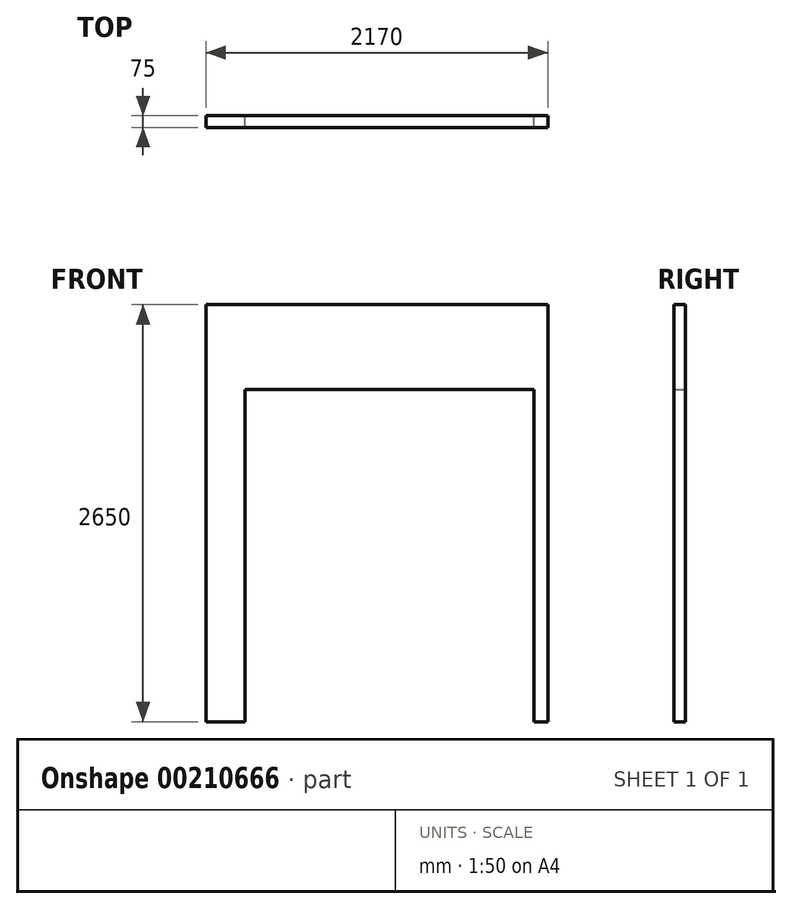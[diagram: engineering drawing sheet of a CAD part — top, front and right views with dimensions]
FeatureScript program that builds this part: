
annotation { "Feature Type Name" : "Feature", "Feature Type Description" : "" }
export const myFeature = defineFeature(function(context is Context, id is Id, definition is map)
    precondition{}
    {
        {
            var Q0;
            Q0=qCreatedBy(makeId("Front.planeOp"),FACE);
            var sketch = newSketch(context, id + "F0", { "sketchPlane" : qUnion([Q0])});
            skLineSegment(sketch, "E0.bottom", {"start": v(0, 0) * mm, "end": v(2170, 0) * mm});
            skLineSegment(sketch, "E0.top", {"start": v(0, 2650) * mm, "end": v(2170, 2650) * mm});
            skLineSegment(sketch, "E0.left", {"start": v(0, 0) * mm, "end": v(0, 2650) * mm});
            skLineSegment(sketch, "E0.right", {"start": v(2170, 0) * mm, "end": v(2170, 2650) * mm});
            skLineSegment(sketch, "E1.bottom", {"start": v(248, 0) * mm, "end": v(2082, 0) * mm});
            skLineSegment(sketch, "E1.top", {"start": v(248, 2110) * mm, "end": v(2082, 2110) * mm});
            skLineSegment(sketch, "E1.left", {"start": v(248, 0) * mm, "end": v(248, 2110) * mm});
            skLineSegment(sketch, "E1.right", {"start": v(2082, 0) * mm, "end": v(2082, 2110) * mm});
            skSolve(sketch);
        }
        {
            var Q0;
            Q0=makeQuery(id+"F0.imprint","IMPRINT",FACE,{"disambiguationData":[TD([[makeQuery(id+"F0.imprint","IMPRINT",EDGE,{"derivedFrom":sQuery(id+"F0.wireOp",EDGE,"E0.bottom")}),1.0]])]});
            extrude(context, id + "F1", {"entities" : qUnion([Q0]), "depth" : 75 * mm});
        }
    });
